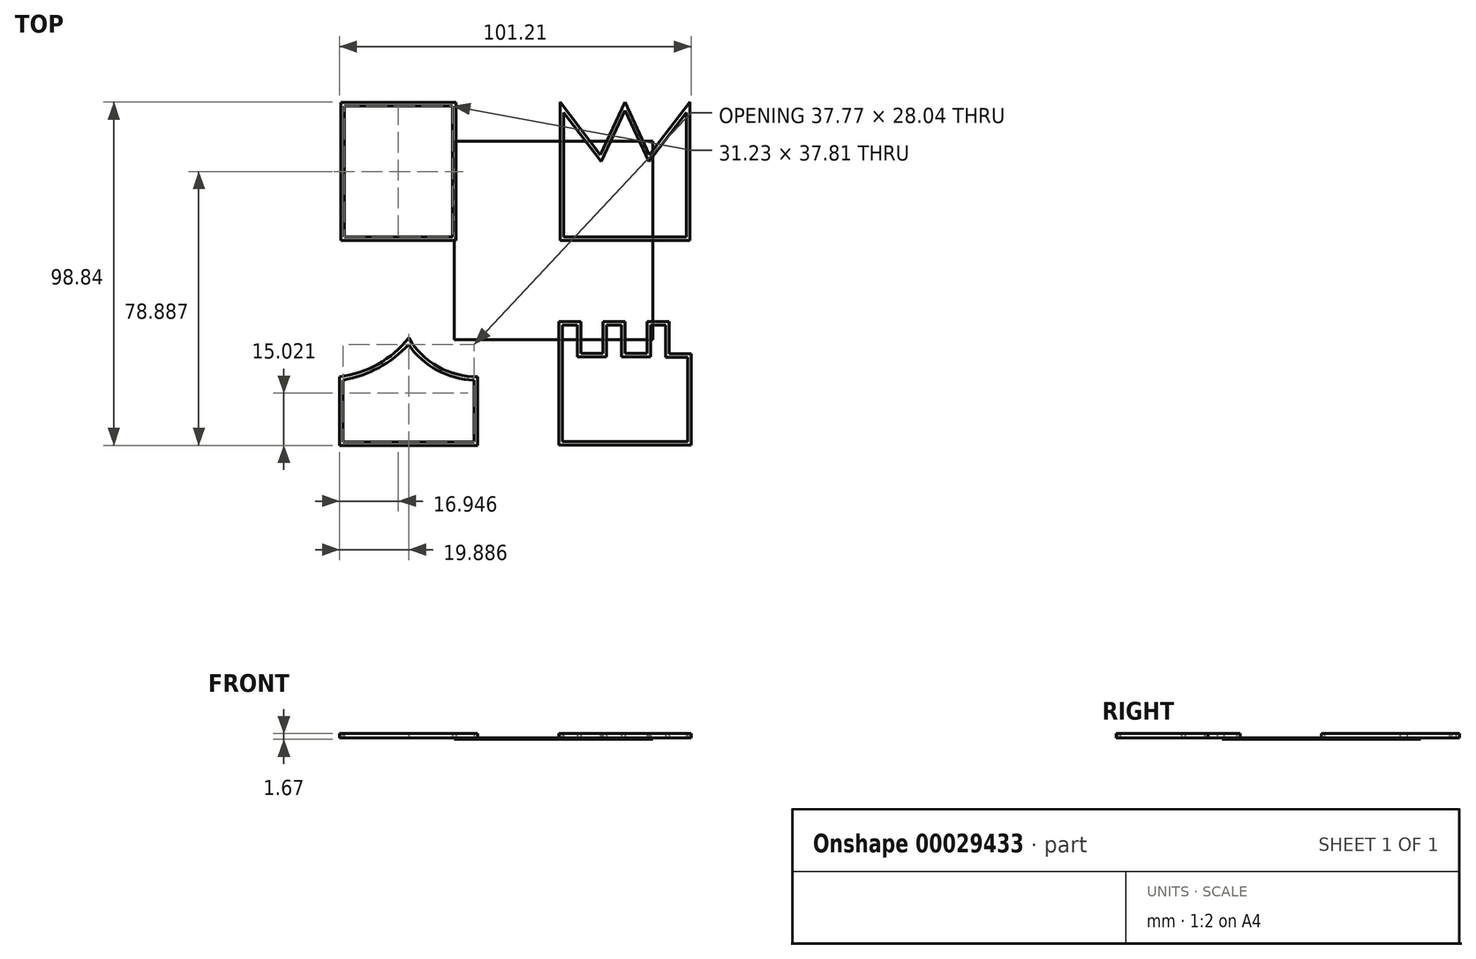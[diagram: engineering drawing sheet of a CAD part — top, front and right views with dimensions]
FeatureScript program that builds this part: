
annotation { "Feature Type Name" : "Feature", "Feature Type Description" : "" }
export const myFeature = defineFeature(function(context is Context, id is Id, definition is map)
    precondition{}
    {
        {
            var Q0;
            Q0=qCreatedBy(makeId("Top.planeOp"),FACE);
            var sketch = newSketch(context, id + "F0", { "sketchPlane" : qUnion([Q0])});
            skLineSegment(sketch, "E0.bottom", {"start": v(-28.58, 28.58) * mm, "end": v(28.58, 28.57) * mm});
            skLineSegment(sketch, "E0.top", {"start": v(-28.57, -28.58) * mm, "end": v(28.58, -28.58) * mm});
            skLineSegment(sketch, "E0.left", {"start": v(-28.57, 28.57) * mm, "end": v(-28.58, -28.58) * mm});
            skLineSegment(sketch, "E0.right", {"start": v(28.58, 28.57) * mm, "end": v(28.58, -28.58) * mm});
            skLineSegment(sketch, "E1", {"start": v(73.4, 0) * mm, "end": v(-187.75, 0) * mm, "construction": true});
            skSolve(sketch);
        }
        {
            var Q0;
            Q0 = qSketchRegion(id + "F0", true);
            extrude(context, id + "F1", {"entities" : qUnion([Q0]), "depth" : 0.4 * mm});
        }
        {
            var Q0;
            Q0=makeQuery(id+"F1.opExtrude","CAP_FACE",FACE,{"disambiguationData":[OSD([sQuery(id+"F0.wireOp",EDGE,"E0.bottom"),sQuery(id+"F0.wireOp",EDGE,"E0.top"),sQuery(id+"F0.wireOp",EDGE,"E0.left"),sQuery(id+"F0.wireOp",EDGE,"E0.right")])],"isStart":false});
            var sketch = newSketch(context, id + "F2", { "sketchPlane" : qUnion([Q0])});
            skLineSegment(sketch, "E2.bottom", {"start": v(-61.28, 39.81) * mm, "end": v(-60.28, 39.81) * mm});
            skLineSegment(sketch, "E2.left", {"start": v(-61.28, 39.81) * mm, "end": v(-61.28, 1) * mm});
            skLineSegment(sketch, "E2.right", {"start": v(-60.28, 38.81) * mm, "end": v(-60.28, 1) * mm});
            skLineSegment(sketch, "E3.bottom", {"start": v(-60.28, 39.81) * mm, "end": v(-28.05, 39.81) * mm});
            skLineSegment(sketch, "E3.top", {"start": v(-60.28, 38.81) * mm, "end": v(-29.05, 38.81) * mm});
            skLineSegment(sketch, "E3.right", {"start": v(-28.05, 39.81) * mm, "end": v(-28.05, 38.81) * mm});
            skLineSegment(sketch, "E4.top", {"start": v(-29.05, 0) * mm, "end": v(-28.05, 0) * mm});
            skLineSegment(sketch, "E4.left", {"start": v(-29.05, 38.81) * mm, "end": v(-29.05, 1) * mm});
            skLineSegment(sketch, "E4.right", {"start": v(-28.05, 38.81) * mm, "end": v(-28.05, 0) * mm});
            skLineSegment(sketch, "E5.bottom", {"start": v(-29.05, 0) * mm, "end": v(-61.28, 0) * mm});
            skLineSegment(sketch, "E5.top", {"start": v(-29.05, 1) * mm, "end": v(-60.28, 1) * mm});
            skLineSegment(sketch, "E5.right", {"start": v(-61.28, 0) * mm, "end": v(-61.28, 1) * mm});
            skLineSegment(sketch, "E6", {"start": v(1.9, 39.86) * mm, "end": v(1.9, 0) * mm});
            skLineSegment(sketch, "E7", {"start": v(1.9, 0) * mm, "end": v(39.2, 0) * mm});
            skLineSegment(sketch, "E8", {"start": v(39.2, 0) * mm, "end": v(39.2, 39.86) * mm});
            skLineSegment(sketch, "E9", {"start": v(39.2, 39.86) * mm, "end": v(27.59, 24.64) * mm});
            skLineSegment(sketch, "E10", {"start": v(27.59, 24.64) * mm, "end": v(20.55, 39.86) * mm});
            skLineSegment(sketch, "E11", {"start": v(20.55, 39.86) * mm, "end": v(13.5, 24.64) * mm});
            skLineSegment(sketch, "E12", {"start": v(13.5, 24.64) * mm, "end": v(1.9, 39.86) * mm});
            skLineSegment(sketch, "E13", {"start": v(20.55, 60.98) * mm, "end": v(20.55, -24.45) * mm, "construction": true});
            skLineSegment(sketch, "E14", {"start": v(-10.85, 39.86) * mm, "end": v(81.44, 39.86) * mm, "construction": true});
            skLineSegment(sketch, "E15.0", {"start": v(20.55, 37.48) * mm, "end": v(13.72, 22.71) * mm});
            skLineSegment(sketch, "E15.1", {"start": v(27.38, 22.71) * mm, "end": v(20.55, 37.48) * mm});
            skLineSegment(sketch, "E15.2", {"start": v(38.2, 36.9) * mm, "end": v(27.38, 22.71) * mm});
            skLineSegment(sketch, "E15.3", {"start": v(38.2, 1) * mm, "end": v(38.2, 36.9) * mm});
            skLineSegment(sketch, "E15.4", {"start": v(2.9, 1) * mm, "end": v(38.2, 1) * mm});
            skLineSegment(sketch, "E15.5", {"start": v(13.72, 22.71) * mm, "end": v(2.9, 36.9) * mm});
            skLineSegment(sketch, "E15.6", {"start": v(2.9, 36.9) * mm, "end": v(2.9, 1) * mm});
            skLineSegment(sketch, "E16.top", {"start": v(-61.6, -58.98) * mm, "end": v(-21.84, -58.98) * mm});
            skLineSegment(sketch, "E16.left", {"start": v(-61.6, -39.17) * mm, "end": v(-61.6, -58.98) * mm});
            skLineSegment(sketch, "E17", {"start": v(-41.72, -65.55) * mm, "end": v(-41.72, -28.07) * mm, "construction": true});
            skLineSegment(sketch, "E18.1", {"start": v(-60.6, -40.17) * mm, "end": v(-60.6, -57.98) * mm});
            skLineSegment(sketch, "E18.2", {"start": v(-60.6, -57.98) * mm, "end": v(-22.84, -57.98) * mm});
            skLineSegment(sketch, "E18.3", {"start": v(-22.84, -40.17) * mm, "end": v(-22.84, -57.98) * mm});
            skPoint(sketch, "E19.MirrorCS.end.orphan", {"position": v(-41.72, -28.07) * mm});
            skPoint(sketch, "E19.MirrorCS.start.orphan", {"position": v(-21.84, -39.17) * mm});
            skLineSegment(sketch, "E20", {"start": v(-21.84, -39.17) * mm, "end": v(-21.84, -58.98) * mm});
            skArc(sketch, "E21", {"start": v(-41.72, -28.07) * mm, "mid": v(-33.29, -36.32) * mm, "end": v(-21.84, -39.17) * mm});
            skArc(sketch, "E22", {"start": v(-61.6, -39.17) * mm, "mid": v(-50.56, -35.6) * mm, "end": v(-41.72, -28.07) * mm});
            skArc(sketch, "E23", {"start": v(-60.6, -40.17) * mm, "mid": v(-50.32, -36.6) * mm, "end": v(-41.72, -29.94) * mm});
            skLineSegment(sketch, "E24.bottom", {"start": v(1.5, -23.3) * mm, "end": v(7.85, -23.3) * mm});
            skLineSegment(sketch, "E24.top", {"start": v(1.5, -58.86) * mm, "end": v(39.6, -58.86) * mm});
            skLineSegment(sketch, "E24.left", {"start": v(1.5, -23.3) * mm, "end": v(1.5, -58.86) * mm});
            skLineSegment(sketch, "E24.right", {"start": v(39.6, -32.58) * mm, "end": v(39.6, -58.86) * mm});
            skLineSegment(sketch, "E25.top", {"start": v(7.85, -32.45) * mm, "end": v(14.2, -32.45) * mm});
            skLineSegment(sketch, "E25.left", {"start": v(7.85, -23.3) * mm, "end": v(7.85, -32.45) * mm});
            skLineSegment(sketch, "E25.right", {"start": v(14.2, -23.3) * mm, "end": v(14.2, -32.45) * mm});
            skLineSegment(sketch, "E26.bottom", {"start": v(20.55, -23.3) * mm, "end": v(20.55, -23.3) * mm});
            skLineSegment(sketch, "E26.top", {"start": v(20.55, -32.45) * mm, "end": v(26.9, -32.45) * mm});
            skLineSegment(sketch, "E26.left", {"start": v(20.55, -23.3) * mm, "end": v(20.55, -32.45) * mm});
            skLineSegment(sketch, "E26.right", {"start": v(26.9, -23.3) * mm, "end": v(26.9, -32.45) * mm});
            skLineSegment(sketch, "E27.top", {"start": v(33.25, -32.58) * mm, "end": v(39.6, -32.58) * mm});
            skLineSegment(sketch, "E27.left", {"start": v(33.25, -23.3) * mm, "end": v(33.25, -32.58) * mm});
            skLineSegment(sketch, "E28.trimOffspring", {"start": v(14.2, -23.3) * mm, "end": v(20.55, -23.3) * mm});
            skLineSegment(sketch, "E29.trimOffspring", {"start": v(26.9, -23.3) * mm, "end": v(33.25, -23.3) * mm});
            skLineSegment(sketch, "E30", {"start": v(2.5, -57.86) * mm, "end": v(38.6, -57.86) * mm});
            skLineSegment(sketch, "E31", {"start": v(2.5, -57.86) * mm, "end": v(2.5, -24.3) * mm});
            skLineSegment(sketch, "E32", {"start": v(2.5, -24.3) * mm, "end": v(6.85, -24.3) * mm});
            skLineSegment(sketch, "E33", {"start": v(6.85, -24.3) * mm, "end": v(6.85, -33.45) * mm});
            skLineSegment(sketch, "E34", {"start": v(6.85, -33.45) * mm, "end": v(15.2, -33.45) * mm});
            skLineSegment(sketch, "E35", {"start": v(15.2, -33.45) * mm, "end": v(15.2, -24.3) * mm});
            skLineSegment(sketch, "E36", {"start": v(15.2, -24.3) * mm, "end": v(19.55, -24.3) * mm});
            skLineSegment(sketch, "E37", {"start": v(19.55, -24.3) * mm, "end": v(19.55, -33.45) * mm});
            skLineSegment(sketch, "E38", {"start": v(19.55, -33.45) * mm, "end": v(27.9, -33.45) * mm});
            skLineSegment(sketch, "E39", {"start": v(27.9, -33.45) * mm, "end": v(27.9, -24.3) * mm});
            skLineSegment(sketch, "E40", {"start": v(27.9, -24.3) * mm, "end": v(32.25, -24.3) * mm});
            skLineSegment(sketch, "E41", {"start": v(32.25, -24.3) * mm, "end": v(32.25, -33.58) * mm});
            skLineSegment(sketch, "E42", {"start": v(32.25, -33.58) * mm, "end": v(38.6, -33.58) * mm});
            skLineSegment(sketch, "E43", {"start": v(38.6, -33.58) * mm, "end": v(38.6, -57.86) * mm});
            skArc(sketch, "E44.0", {"start": v(-41.72, -29.94) * mm, "mid": v(-33.52, -37.34) * mm, "end": v(-22.84, -40.17) * mm});
            skSolve(sketch);
        }
        {
            var Q0;
            Q0 = qSketchRegion(id + "F2", true);
            extrude(context, id + "F3", {"entities" : qUnion([Q0]), "operationType" : NewBodyOperationType.ADD, "depth" : 1.27 * mm});
        }
    });
